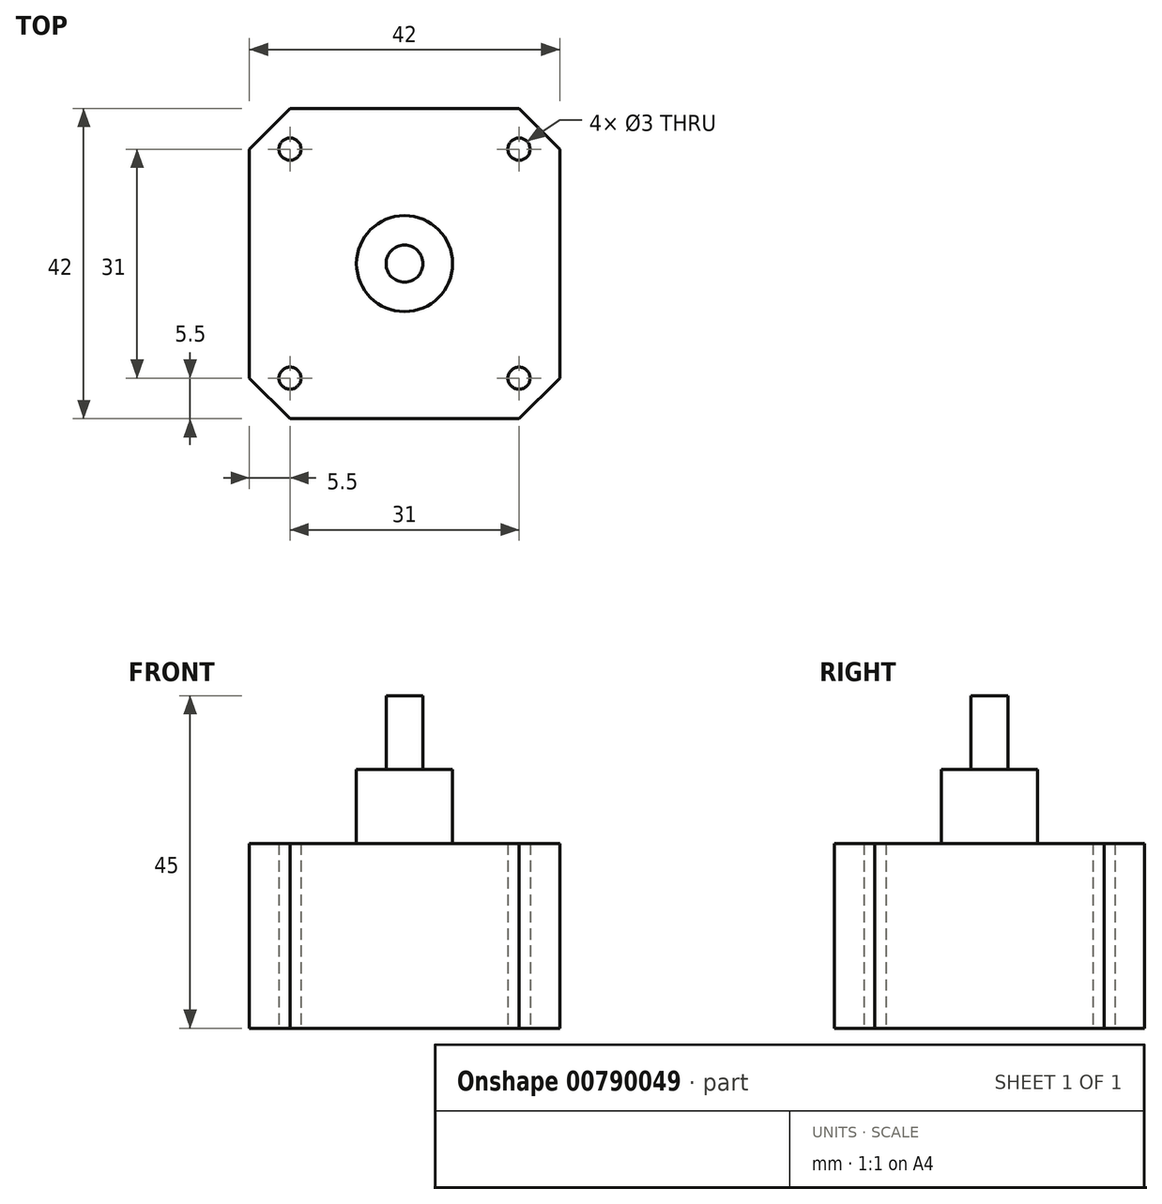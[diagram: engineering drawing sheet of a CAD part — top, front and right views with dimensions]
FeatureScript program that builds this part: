
annotation { "Feature Type Name" : "Feature", "Feature Type Description" : "" }
export const myFeature = defineFeature(function(context is Context, id is Id, definition is map)
    precondition{}
    {
        {
            var Q0;
            Q0=qCreatedBy(makeId("Top.planeOp"),FACE);
            var sketch = newSketch(context, id + "F0", { "sketchPlane" : qUnion([Q0])});
            skCircle(sketch, "E0", {"center": v(0, 0) * mm, "radius": 2.5 * mm});
            skLineSegment(sketch, "E1.bottom", {"start": v(-15.5, 21) * mm, "end": v(15.5, 21) * mm});
            skLineSegment(sketch, "E1.top", {"start": v(-15.5, -21) * mm, "end": v(15.5, -21) * mm});
            skLineSegment(sketch, "E1.left", {"start": v(-21, 15.5) * mm, "end": v(-21, -15.5) * mm});
            skLineSegment(sketch, "E1.right", {"start": v(21, 15.5) * mm, "end": v(21, -15.5) * mm});
            skCircle(sketch, "E2", {"center": v(-15.5, 15.5) * mm, "radius": 1.5 * mm});
            skCircle(sketch, "E3", {"center": v(15.5, 15.5) * mm, "radius": 1.5 * mm});
            skCircle(sketch, "E4", {"center": v(15.5, -15.5) * mm, "radius": 1.5 * mm});
            skCircle(sketch, "E5", {"center": v(-15.5, -15.5) * mm, "radius": 1.5 * mm});
            skLineSegment(sketch, "E6", {"start": v(-15.5, 15.5) * mm, "end": v(-15.5, -15.5) * mm, "construction": true});
            skLineSegment(sketch, "E7", {"start": v(15.5, -15.5) * mm, "end": v(-15.5, -15.5) * mm, "construction": true});
            skLineSegment(sketch, "E8", {"start": v(15.5, -15.5) * mm, "end": v(15.5, 15.5) * mm, "construction": true});
            skLineSegment(sketch, "E9", {"start": v(15.5, 15.5) * mm, "end": v(-15.5, 15.5) * mm, "construction": true});
            skPoint(sketch, "E10", {"position": v(15.5, 0) * mm});
            skPoint(sketch, "E11", {"position": v(0, 15.5) * mm});
            skLineSegment(sketch, "E12", {"start": v(-21, 15.5) * mm, "end": v(-15.5, 21) * mm});
            skLineSegment(sketch, "E13", {"start": v(15.5, 21) * mm, "end": v(21, 15.5) * mm});
            skLineSegment(sketch, "E14", {"start": v(21, -15.5) * mm, "end": v(15.5, -21) * mm});
            skLineSegment(sketch, "E15", {"start": v(-21, -15.5) * mm, "end": v(-15.5, -21) * mm});
            skPoint(sketch, "E16", {"position": v(0, 21) * mm});
            skPoint(sketch, "E17", {"position": v(-21, 0) * mm});
            skCircle(sketch, "E18", {"center": v(0, 0) * mm, "radius": 6.5 * mm});
            skSolve(sketch);
        }
        {
            var Q0;
            {var subQ5=sQuery(id+"F0.wireOp",EDGE,"c1u5kAW5-9cBP-avJs-xcup-djQMre1z8to3.bottom");Q0=makeQuery(id+"F0.imprint","IMPRINT",FACE,{"disambiguationData":[TD([[makeQuery(id+"F0.imprint","IMPRINT",EDGE,{"derivedFrom":subQ5}),1.0]])]});}
            var Q1;
            {var subQ5=sQuery(id+"F0.wireOp",EDGE,"c1u5kAW5-9cBP-avJs-xcup-djQMre1z8to3.bottom");Q1=makeQuery(id+"F0.imprint","IMPRINT",FACE,{"disambiguationData":[TD([[makeQuery(id+"F0.imprint","IMPRINT",EDGE,{"derivedFrom":subQ5}),-1.0]])]});}
            var Q2;
            Q2=makeQuery(id+"F0.imprint","IMPRINT",FACE,{"disambiguationData":[TD([[makeQuery(id+"F0.imprint","IMPRINT",EDGE,{"derivedFrom":sQuery(id+"F0.wireOp",EDGE,"E1.bottom")}),-1.0]])]});
            extrude(context, id + "F1", {"entities" : qUnion([Q0, Q1, Q2]), "depth" : 25 * mm, "offsetDistance" : 25 * mm});
        }
        {
            var Q0;
            Q0=makeQuery(id+"F0.imprint","IMPRINT",FACE,{"disambiguationData":[TD([[makeQuery(id+"F0.imprint","IMPRINT",EDGE,{"derivedFrom":sQuery(id+"F0.wireOp",EDGE,"E0")}),-1.0]])]});
            extrude(context, id + "F2", {"entities" : qUnion([Q0]), "operationType" : NewBodyOperationType.ADD, "depth" : 35 * mm, "offsetDistance" : 25 * mm});
        }
        {
            var Q0;
            Q0=makeQuery(id+"F0.imprint","IMPRINT",FACE,{"disambiguationData":[TD([[makeQuery(id+"F0.imprint","IMPRINT",EDGE,{"derivedFrom":sQuery(id+"F0.wireOp",EDGE,"E0")}),1.0]])]});
            extrude(context, id + "F3", {"entities" : qUnion([Q0]), "operationType" : NewBodyOperationType.ADD, "depth" : 45 * mm, "offsetDistance" : 25 * mm});
        }
    });
